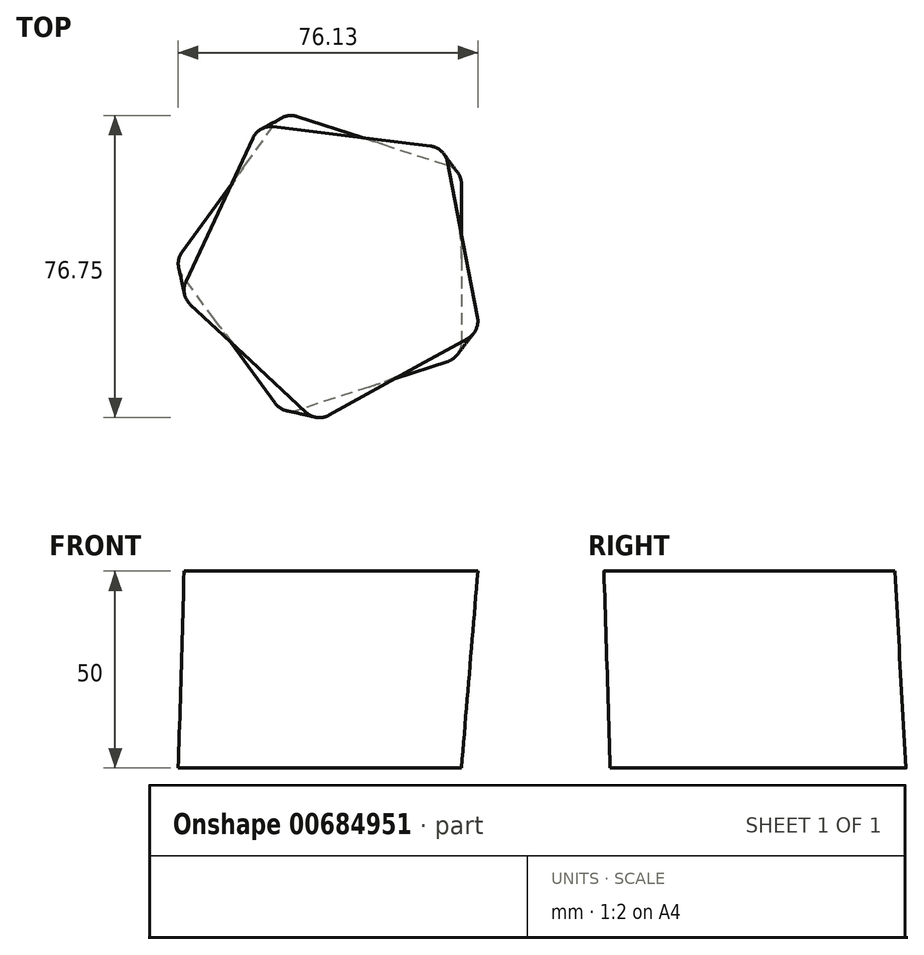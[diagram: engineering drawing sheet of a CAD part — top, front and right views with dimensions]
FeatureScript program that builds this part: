
annotation { "Feature Type Name" : "Feature", "Feature Type Description" : "" }
export const myFeature = defineFeature(function(context is Context, id is Id, definition is map)
    precondition{}
    {
        {
            var Q0;
            Q0=qCreatedBy(makeId("Top.planeOp"),FACE);
            var sketch = newSketch(context, id + "F0", { "sketchPlane" : qUnion([Q0])});
            skLineSegment(sketch, "E0.0", {"start": v(32.7, 20.13) * mm, "end": v(32.7, -20.13) * mm});
            skLineSegment(sketch, "E0.1", {"start": v(29.25, -24.89) * mm, "end": v(-9.04, -37.33) * mm});
            skLineSegment(sketch, "E0.2", {"start": v(-14.63, -35.51) * mm, "end": v(-38.3, -2.94) * mm});
            skLineSegment(sketch, "E0.3", {"start": v(-38.3, 2.94) * mm, "end": v(-14.63, 35.51) * mm});
            skLineSegment(sketch, "E0.4", {"start": v(-9.04, 37.33) * mm, "end": v(29.25, 24.89) * mm});
            skPoint(sketch, "E1.visualSharp", {"position": v(-12.5, 38.45) * mm});
            skArc(sketch, "E1.filletArc", {"start": v(-9.04, 37.33) * mm, "mid": v(-12.13, 37.33) * mm, "end": v(-14.63, 35.51) * mm});
            skPoint(sketch, "E2.visualSharp", {"position": v(32.7, 23.76) * mm});
            skArc(sketch, "E2.filletArc", {"start": v(32.7, 20.13) * mm, "mid": v(31.75, 23.07) * mm, "end": v(29.25, 24.89) * mm});
            skPoint(sketch, "E3.visualSharp", {"position": v(32.7, -23.76) * mm});
            skArc(sketch, "E3.filletArc", {"start": v(29.25, -24.89) * mm, "mid": v(31.75, -23.07) * mm, "end": v(32.7, -20.13) * mm});
            skPoint(sketch, "E4.visualSharp", {"position": v(-12.5, -38.45) * mm});
            skArc(sketch, "E4.filletArc", {"start": v(-14.63, -35.51) * mm, "mid": v(-12.13, -37.33) * mm, "end": v(-9.04, -37.33) * mm});
            skPoint(sketch, "E5.visualSharp", {"position": v(-40.43, 0) * mm});
            skArc(sketch, "E5.filletArc", {"start": v(-38.3, 2.94) * mm, "mid": v(-39.25, 0) * mm, "end": v(-38.3, -2.94) * mm});
            skSolve(sketch);
        }
        {
            var Q0;
            Q0=qCreatedBy(makeId("Top.planeOp"),FACE);
            cPlane(context, id + "F1", {"entities" : qUnion([Q0]), "cplaneType" : CPlaneType.OFFSET, "offset" : 50 * mm, "width" : 150 * mm, "height" : 150 * mm});
        }
        {
            var Q0;
            Q0=qCreatedBy(id+"F1.planeOp",FACE);
            var sketch = newSketch(context, id + "F2", { "sketchPlane" : qUnion([Q0])});
            skLineSegment(sketch, "E6.0", {"start": v(-37.31, -4.6) * mm, "end": v(-20.3, 31.88) * mm});
            skLineSegment(sketch, "E6.1", {"start": v(-15.16, 34.73) * mm, "end": v(24.8, 29.83) * mm});
            skLineSegment(sketch, "E6.2", {"start": v(29.1, 25.82) * mm, "end": v(36.79, -13.7) * mm});
            skLineSegment(sketch, "E6.3", {"start": v(34.3, -19.03) * mm, "end": v(-0.91, -38.55) * mm});
            skLineSegment(sketch, "E6.4", {"start": v(-6.75, -37.84) * mm, "end": v(-36.2, -10.38) * mm});
            skPoint(sketch, "E7.visualSharp", {"position": v(-4.09, -40.31) * mm});
            skArc(sketch, "E7.filletArc", {"start": v(-6.75, -37.84) * mm, "mid": v(-3.95, -39.14) * mm, "end": v(-0.91, -38.55) * mm});
            skPoint(sketch, "E8.visualSharp", {"position": v(-38.85, -7.9) * mm});
            skArc(sketch, "E8.filletArc", {"start": v(-37.31, -4.6) * mm, "mid": v(-37.7, -7.67) * mm, "end": v(-36.2, -10.38) * mm});
            skPoint(sketch, "E9.visualSharp", {"position": v(-18.76, 35.18) * mm});
            skArc(sketch, "E9.filletArc", {"start": v(-15.16, 34.73) * mm, "mid": v(-18.2, 34.14) * mm, "end": v(-20.3, 31.88) * mm});
            skPoint(sketch, "E10.visualSharp", {"position": v(28.41, 29.38) * mm});
            skArc(sketch, "E10.filletArc", {"start": v(29.1, 25.82) * mm, "mid": v(27.6, 28.52) * mm, "end": v(24.8, 29.83) * mm});
            skPoint(sketch, "E11.visualSharp", {"position": v(37.48, -17.27) * mm});
            skArc(sketch, "E11.filletArc", {"start": v(34.3, -19.03) * mm, "mid": v(36.4, -16.77) * mm, "end": v(36.79, -13.7) * mm});
            skPoint(sketch, "E12", {"position": v(0.44, 0) * mm});
            skSolve(sketch);
        }
        {
            var Q0;
            Q0=makeQuery(id+"F0.imprint","IMPRINT",FACE,{"disambiguationData":[TD([[makeQuery(id+"F0.imprint","IMPRINT",EDGE,{"derivedFrom":sQuery(id+"F0.wireOp",EDGE,"E0.0")}),-1.0]])]});
            var Q1;
            Q1=makeQuery(id+"F2.imprint","IMPRINT",FACE,{"disambiguationData":[TD([[makeQuery(id+"F2.imprint","IMPRINT",EDGE,{"derivedFrom":sQuery(id+"F2.wireOp",EDGE,"E6.0")}),-1.0]])]});
            loft(context, id + "F3", {"sheetProfilesArray" : [{ "sheetProfileEntities" : qUnion([Q0]) }, { "sheetProfileEntities" : qUnion([Q1]) }]});
        }
    });
